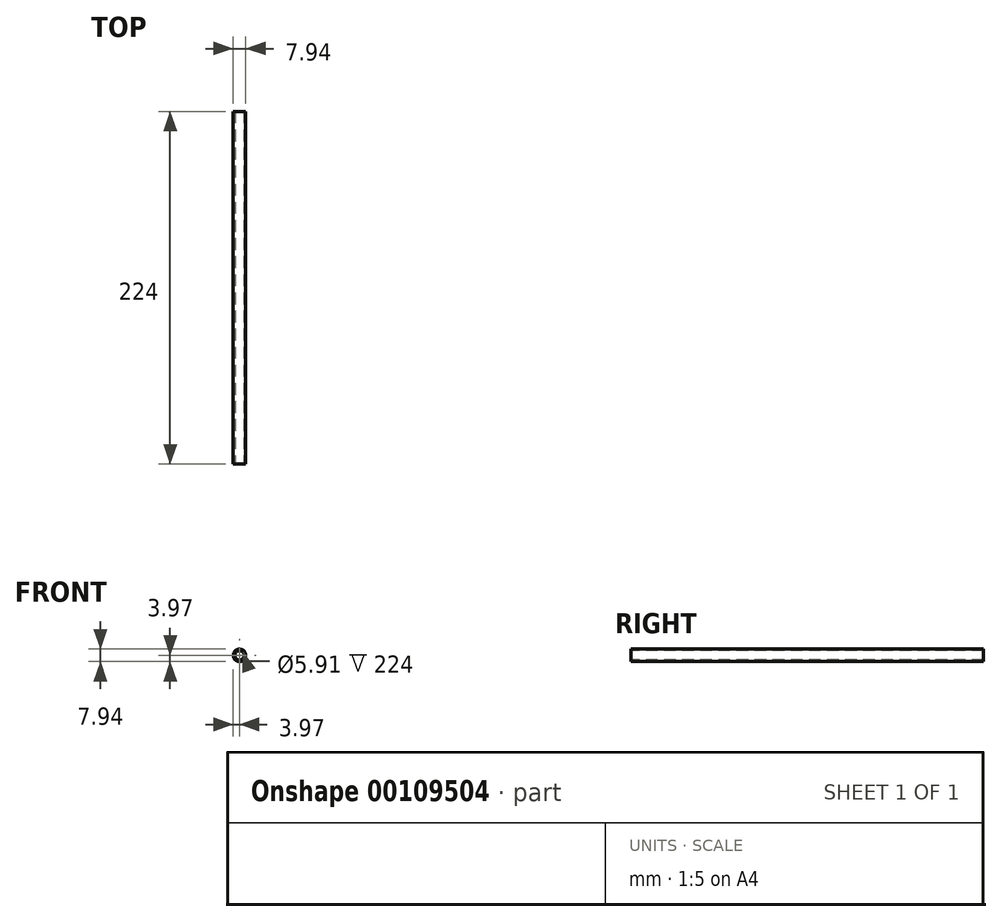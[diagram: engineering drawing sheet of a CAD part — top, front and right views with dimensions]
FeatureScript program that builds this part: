
annotation { "Feature Type Name" : "Feature", "Feature Type Description" : "" }
export const myFeature = defineFeature(function(context is Context, id is Id, definition is map)
    precondition{}
    {
        {
            var Q0;
            Q0=qCreatedBy(makeId("Top.planeOp"),FACE);
            var sketch = newSketch(context, id + "F0", { "sketchPlane" : qUnion([Q0])});
            skLineSegment(sketch, "E0.bottom", {"start": v(2.95, 0) * mm, "end": v(3.97, 0) * mm});
            skLineSegment(sketch, "E0.top", {"start": v(2.95, 224) * mm, "end": v(3.97, 224) * mm});
            skLineSegment(sketch, "E0.left", {"start": v(2.95, 0) * mm, "end": v(2.95, 224) * mm});
            skLineSegment(sketch, "E0.right", {"start": v(3.97, 0) * mm, "end": v(3.97, 224) * mm});
            skLineSegment(sketch, "E1", {"start": v(0, 0) * mm, "end": v(0, 224) * mm, "construction": true});
            skSolve(sketch);
        }
        {
            var Q0;
            Q0=qSketchRegion(id+"F0",true);
            var Q1;
            Q1=sQuery(id+"F0.wireOp",EDGE,"E1");
            revolve(context, id + "F1", {"entities" : qUnion([Q0]), "axis" : qUnion([Q1]), "revolveType" : RevolveType.FULL});
        }
    });
